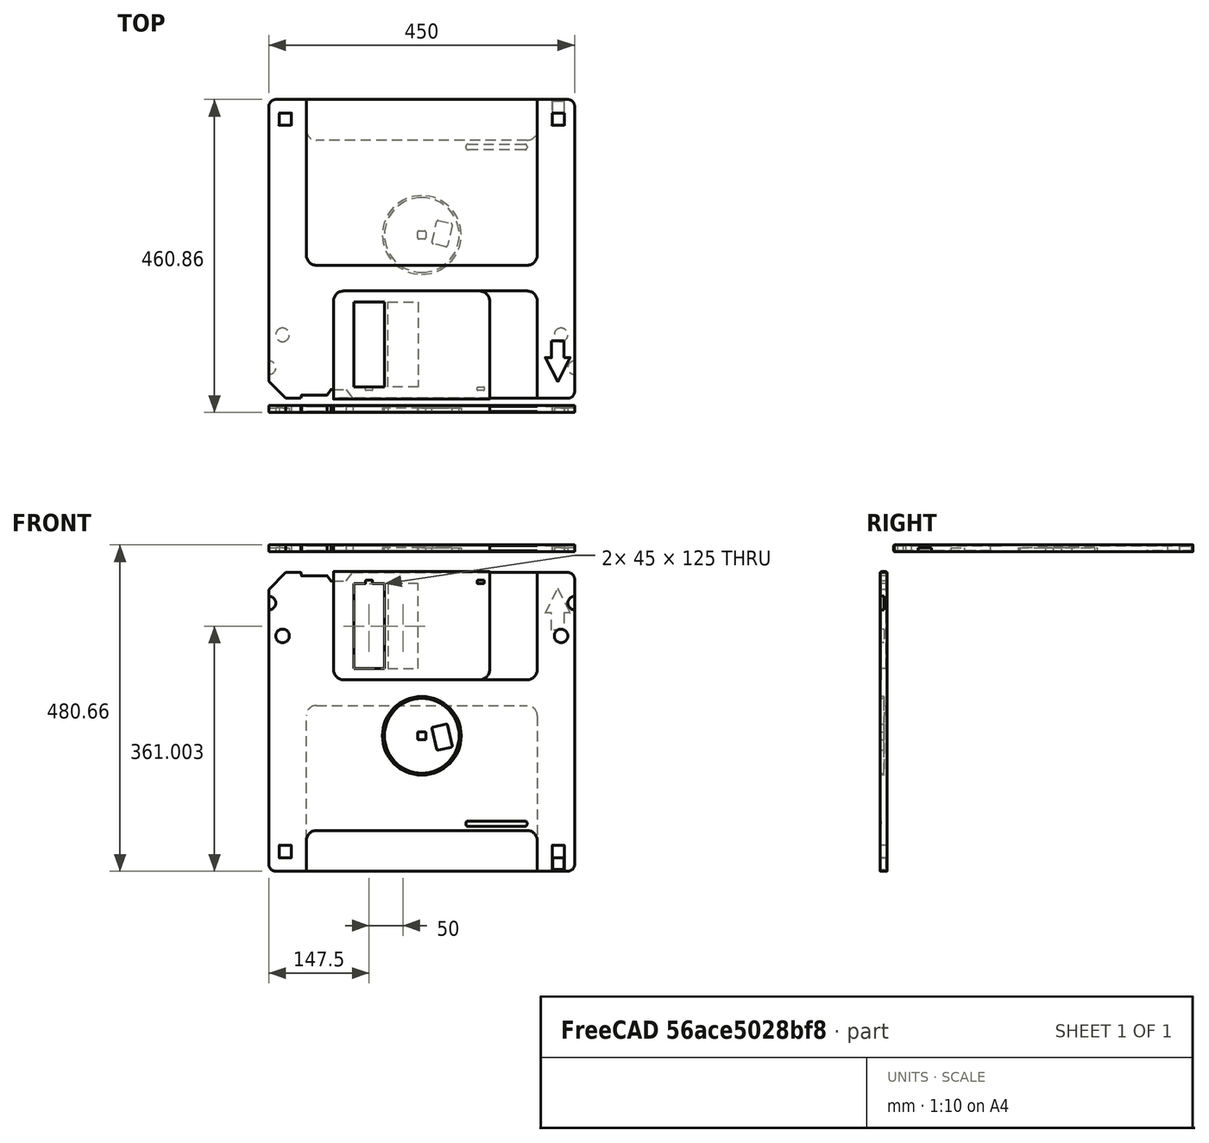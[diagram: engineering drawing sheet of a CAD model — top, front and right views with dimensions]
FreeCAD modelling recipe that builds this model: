
FCSTD DOCUMENT  (FreeCAD 1.0R39285 (Git))
Label: floppy_disk_coaster_Stand_01
License: CERN Open Hardware Licence permissive
LicenseURL: https://cern-ohl.web.cern.ch/
objects: Part::Feature×4, Sketcher::SketchObject×1, PartDesign::Body×1, App::Part×1, Part::FeaturePython×1
note: 8 computed .brp shape members not serialized (recipe doc carries the construction recipe); baked Part::Feature solids carry a one-line shape summary decoded from their .brp

FEATURE [Sketcher::SketchObject] Sketch
  ArcFitTolerance = 1e-06
  AttachmentSupport = -> [XY_Plane]
  FullyConstrained = false
  MakeInternals = false
  MapMode = 5
  sketch-geometry (4):
    g0: LineSegment StartX=-0.098219 StartY=20.6145 StartZ=0 EndX=449.902 EndY=20.6145 EndZ=0
    g1: LineSegment StartX=449.902 StartY=20.6145 StartZ=0 EndX=449.902 EndY=460.615 EndZ=0
    g2: LineSegment StartX=449.902 StartY=460.615 StartZ=0 EndX=-0.098219 EndY=460.615 EndZ=0
    g3: LineSegment StartX=-0.098219 StartY=460.615 StartZ=0 EndX=-0.098219 EndY=20.6145 EndZ=0
  constraints (10):
    c: Coincident(g0,g1)
    c: Coincident(g1,g2)
    c: Coincident(g2,g3)
    c: Coincident(g3,g0)
    c: Horizontal(g0)
    c: Horizontal(g2)
    c: Vertical(g1)
    c: Vertical(g3)
    c: DistanceX(g0,g0) = 450
    c: DistanceY(g1,g1) = 440
FEATURE [PartDesign::Body] Body
  AllowCompound = false
  Group = -> [Sketch]
  Origin = -> Origin
FEATURE [Part::Feature] Part__Feature  label="Disket 01"
  shape: bbox 18 x 8.2 x 18 mm, 10 faces (baked)
FEATURE [Part::Feature] Part__Feature001  label="Disket 002"
  shape: bbox 451.6 x 10 x 441.6 mm, 173 faces (baked)
FEATURE [Part::Feature] Part__Feature002  label="Disket 003"
  shape: bbox 230 x 10 x 159.2 mm, 50 faces (baked)
FEATURE [Part::Feature] Part__Feature003  label="Disket 004"
  shape: bbox 119.1 x 6 x 119.1 mm, 40 faces (baked)
FEATURE [App::Part] Disket_01  label="Disket 005"
  Group = -> [Part__Feature,Part__Feature001,Part__Feature002,Part__Feature003]
  Origin = -> Origin001
  Placement = pos=(0,0,0) rot=(-1,0,0;4.71239rad)
FEATURE [Part::FeaturePython] Clone  label="Disket 006"  # Draft clone (typed FeaturePython)
  AttacherType = Attacher::AttachEngine3D
  Fuse = false
  Objects = -> [Disket_01]
  Placement = pos=(0,0,10) rot=(-1,0,0;4.71239rad)
  Scale = (1,1,1)
